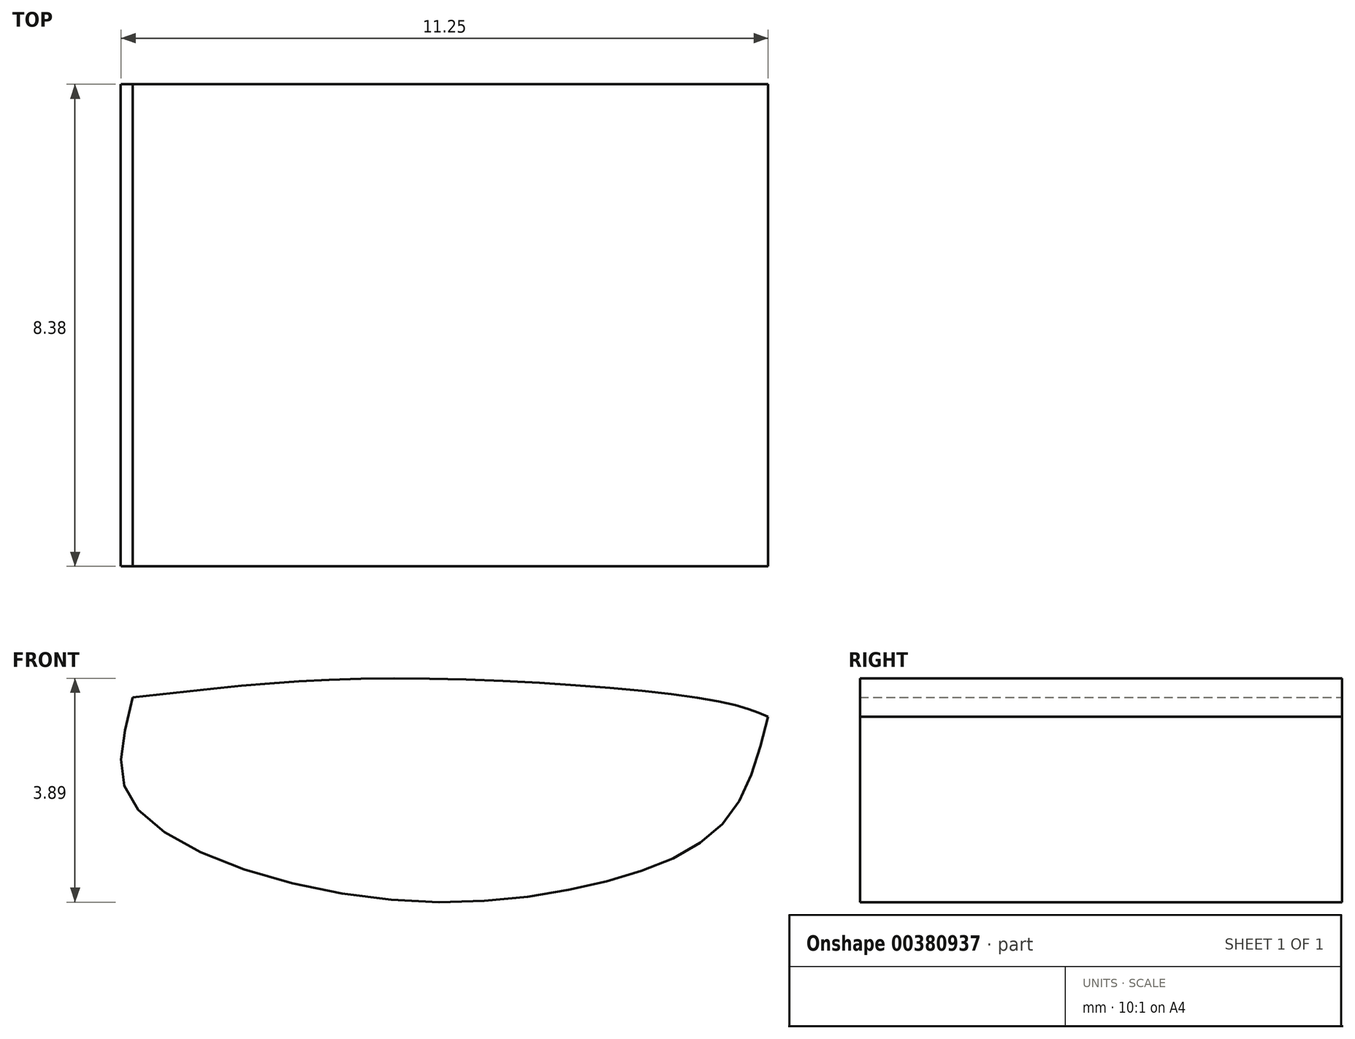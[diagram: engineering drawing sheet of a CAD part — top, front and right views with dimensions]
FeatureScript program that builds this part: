
annotation { "Feature Type Name" : "Feature", "Feature Type Description" : "" }
export const myFeature = defineFeature(function(context is Context, id is Id, definition is map)
    precondition{}
    {
        {
            var Q0;
            Q0=qCreatedBy(makeId("Front.planeOp"),FACE);
            var sketch = newSketch(context, id + "F0", { "sketchPlane" : qUnion([Q0])});
            skFitSpline(sketch, "E0", {"points": [v(-2, -17.57) * mm, v(2.54, -17.24) * mm, v(8.19, -17.64) * mm, v(9.05, -17.9) * mm], "startDerivative": vector(10.89, 1.25) * mm, "endDerivative": vector(3.69, -1.56) * mm});
            skFitSpline(sketch, "E1", {"points": [v(-2, -17.57) * mm, v(-2, -19.4) * mm, v(1.94, -21.03) * mm, v(6.26, -20.76) * mm, v(8.32, -19.7) * mm, v(9.05, -17.9) * mm], "startDerivative": vector(-3.27, -13.77) * mm, "endDerivative": vector(2.94, 11.94) * mm});
            skSolve(sketch);
        }
        {
            var Q0;
            Q0=makeQuery(id+"F0.imprint","IMPRINT",FACE,{"disambiguationData":[TD([[makeQuery(id+"F0.imprint","IMPRINT",EDGE,{"derivedFrom":sQuery(id+"F0.wireOp",EDGE,"E0")}),-1.0]])]});
            extrude(context, id + "F1", {"entities" : qUnion([Q0]), "depth" : 8.38 * mm});
        }
    });
